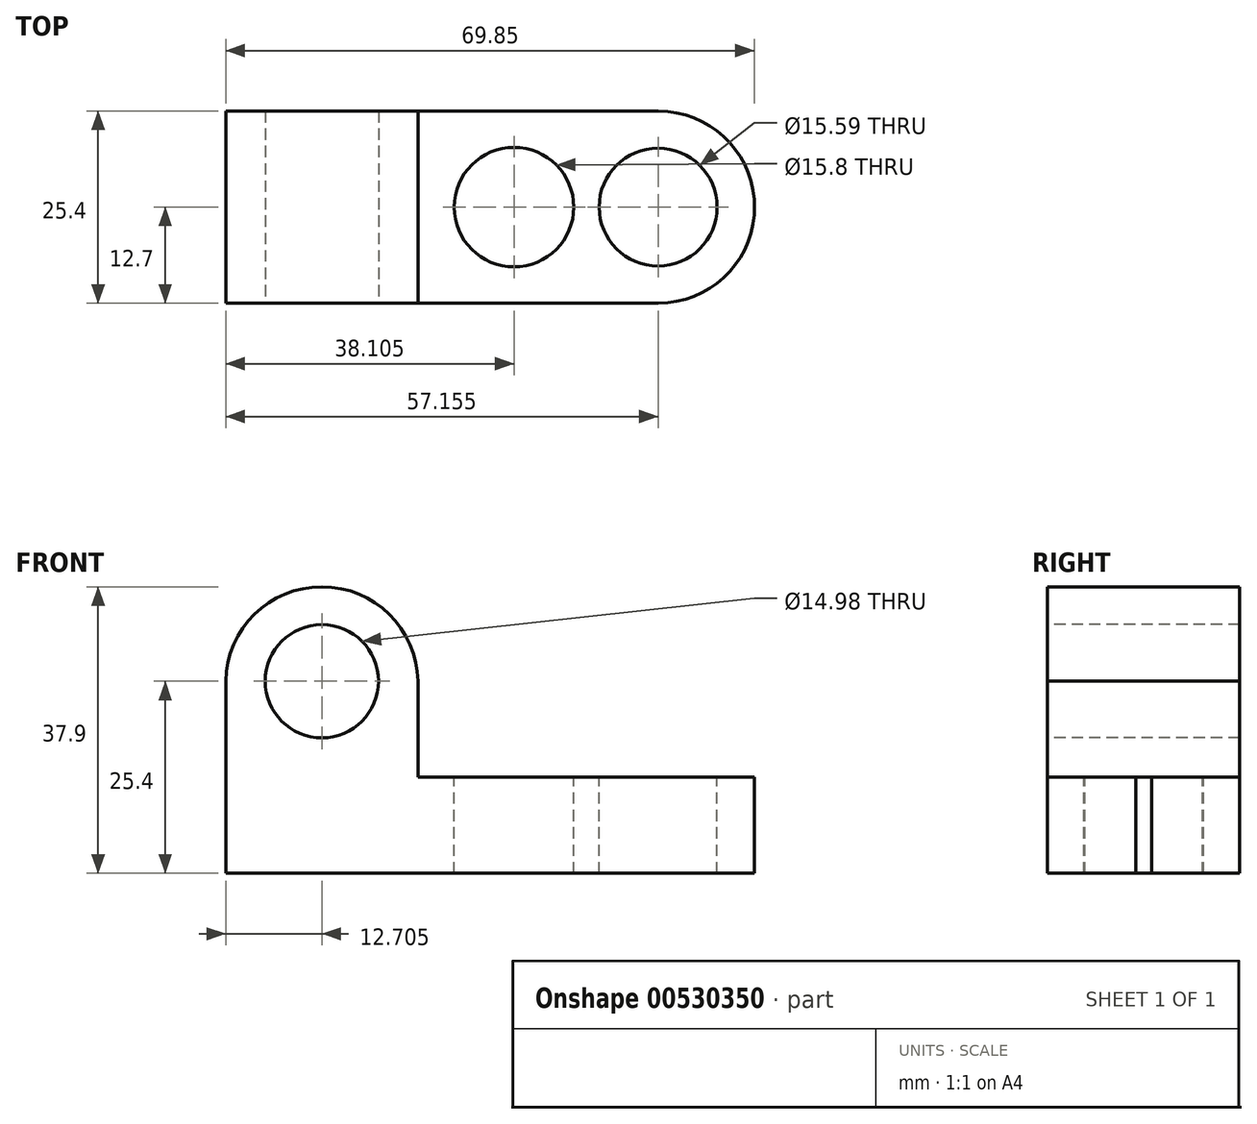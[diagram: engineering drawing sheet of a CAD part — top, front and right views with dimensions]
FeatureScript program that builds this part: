
annotation { "Feature Type Name" : "Feature", "Feature Type Description" : "" }
export const myFeature = defineFeature(function(context is Context, id is Id, definition is map)
    precondition{}
    {
        {
            var Q0;
            Q0=qCreatedBy(makeId("Front.planeOp"),FACE);
            var sketch = newSketch(context, id + "F0", { "sketchPlane" : qUnion([Q0])});
            skLineSegment(sketch, "E0", {"start": v(-78.95, 38.1) * mm, "end": v(-78.95, 0) * mm});
            skLineSegment(sketch, "E1", {"start": v(-78.95, 0) * mm, "end": v(-9.1, 0) * mm});
            skLineSegment(sketch, "E2", {"start": v(-9.1, 0) * mm, "end": v(-9.1, 12.7) * mm});
            skLineSegment(sketch, "E3", {"start": v(-9.1, 12.7) * mm, "end": v(-53.55, 12.7) * mm});
            skLineSegment(sketch, "E4", {"start": v(-53.55, 12.7) * mm, "end": v(-53.55, 38.1) * mm});
            skLineSegment(sketch, "E5", {"start": v(-53.55, 38.1) * mm, "end": v(-78.95, 38.1) * mm});
            skSolve(sketch);
        }
        {
            var Q0;
            Q0 = qSketchRegion(id + "F0", true);
            extrude(context, id + "F1", {"entities" : qUnion([Q0]), "depth" : 25.4 * mm, "offsetDistance" : 25.4 * mm});
        }
        {
            var Q0;
            Q0=makeQuery(id+"F1.opExtrude","CAP_FACE",FACE,{"disambiguationData":[OSD([sQuery(id+"F0.wireOp",EDGE,"E0"),sQuery(id+"F0.wireOp",EDGE,"E1"),sQuery(id+"F0.wireOp",EDGE,"E2"),sQuery(id+"F0.wireOp",EDGE,"E3"),sQuery(id+"F0.wireOp",EDGE,"E4"),sQuery(id+"F0.wireOp",EDGE,"E5")])],"isStart":false});
            var sketch = newSketch(context, id + "F2", { "sketchPlane" : qUnion([Q0])});
            skCircle(sketch, "E6", {"center": v(-66.25, 25.4) * mm, "radius": 7.5 * mm});
            skSolve(sketch);
        }
        {
            var Q0;
            Q0=makeQuery(id+"F2.imprint","IMPRINT",FACE,{"disambiguationData":[TD([[makeQuery(id+"F2.imprint","IMPRINT",EDGE,{"derivedFrom":sQuery(id+"F2.wireOp",EDGE,"E6")}),1.0]])]});
            extrude(context, id + "F3", {"entities" : qUnion([Q0]), "operationType" : NewBodyOperationType.REMOVE, "endBound" : BoundingType.THROUGH_ALL, "oppositeDirection" : true, "depth" : 25.4 * mm, "offsetDistance" : 25.4 * mm});
        }
        {
            var Q0;
            Q0=makeQuery(id+"F1.opExtrude","CAP_FACE",FACE,{"disambiguationData":[OSD([sQuery(id+"F0.wireOp",EDGE,"E0"),sQuery(id+"F0.wireOp",EDGE,"E1"),sQuery(id+"F0.wireOp",EDGE,"E2"),sQuery(id+"F0.wireOp",EDGE,"E3"),sQuery(id+"F0.wireOp",EDGE,"E4"),sQuery(id+"F0.wireOp",EDGE,"E5")])],"isStart":false});
            var sketch = newSketch(context, id + "F4", { "sketchPlane" : qUnion([Q0])});
            skArc(sketch, "E7", {"start": v(-53.55, 25.4) * mm, "mid": v(-66.25, 37.9) * mm, "end": v(-78.95, 25.4) * mm});
            skSolve(sketch);
        }
        {
            var Q0;
            Q0 = qSketchRegion(id + "F4", true);
            var Q1;
            {var subQ0=sQuery(id+"F4.wireOp",EDGE,"E7");Q1=makeQuery(id+"F4.imprint","IMPRINT",FACE,{"disambiguationData":[TD([[makeQuery(id+"F4.imprint","IMPRINT",EDGE,{"derivedFrom":subQ0}),-1.0]])]});}
            extrude(context, id + "F5", {"entities" : qUnion([Q0, Q1]), "operationType" : NewBodyOperationType.REMOVE, "endBound" : BoundingType.THROUGH_ALL, "oppositeDirection" : true, "depth" : 25.4 * mm, "offsetDistance" : 25.4 * mm});
        }
        {
            var Q0;
            Q0=makeQuery(id+"F1.opExtrude","SWEPT_FACE",FACE,{"disambiguationData":[OSD([sQuery(id+"F0.wireOp",EDGE,"E3")])]});
            var sketch = newSketch(context, id + "F6", { "sketchPlane" : qUnion([Q0])});
            skCircle(sketch, "E8", {"center": v(-40.85, -12.7) * mm, "radius": 7.9 * mm});
            skCircle(sketch, "E9", {"center": v(-21.8, -12.7) * mm, "radius": 7.8 * mm});
            skSolve(sketch);
        }
        {
            var Q0;
            Q0=makeQuery(id+"F6.imprint","IMPRINT",FACE,{"disambiguationData":[TD([[makeQuery(id+"F6.imprint","IMPRINT",EDGE,{"derivedFrom":sQuery(id+"F6.wireOp",EDGE,"E8")}),1.0]])]});
            var Q1;
            Q1=makeQuery(id+"F6.imprint","IMPRINT",FACE,{"disambiguationData":[TD([[makeQuery(id+"F6.imprint","IMPRINT",EDGE,{"derivedFrom":sQuery(id+"F6.wireOp",EDGE,"E9")}),1.0]])]});
            extrude(context, id + "F7", {"entities" : qUnion([Q0, Q1]), "operationType" : NewBodyOperationType.REMOVE, "endBound" : BoundingType.THROUGH_ALL, "oppositeDirection" : true, "depth" : 25.4 * mm, "offsetDistance" : 25.4 * mm});
        }
        {
            var Q0;
            Q0=makeQuery(id+"F1.opExtrude","SWEPT_FACE",FACE,{"disambiguationData":[OSD([sQuery(id+"F0.wireOp",EDGE,"E3")])]});
            var sketch = newSketch(context, id + "F8", { "sketchPlane" : qUnion([Q0])});
            skLineSegment(sketch, "E10", {"start": v(-40.69, -20.6) * mm, "end": v(-20.89, -20.44) * mm});
            skLineSegment(sketch, "E11", {"start": v(-40.9, -4.8) * mm, "end": v(-21.75, -4.9) * mm});
            skSolve(sketch);
        }
        {
            var Q0;
            Q0 = qSketchRegion(id + "F8", true);
            var Q1;
            {var subQ0=sQuery(id+"F8.wireOp",EDGE,"E10");var subQ1=makeQuery(id+"F7.boolean.opBoolean","COPY",EDGE,{"derivedFrom":makeQuery(id+"F7.opExtrude","CAP_EDGE",EDGE,{"disambiguationData":[OSD([sQuery(id+"F6.wireOp",EDGE,"E8")])],"isStart":true})});var subQ2=makeQuery(id+"F8.imprint","INTERSECT",VERTEX,{"derivedFrom":[subQ1,subQ0]});Q1=makeQuery(id+"F8.imprint","IMPRINT",FACE,{"disambiguationData":[TD([[makeQuery(id+"F8.imprint","IMPRINT",EDGE,{"disambiguationData":[TD([[subQ2,-1.0]])],"derivedFrom":subQ0}),1.0]])]});}
            extrude(context, id + "F9", {"entities" : qUnion([Q0, Q1]), "operationType" : NewBodyOperationType.REMOVE, "endBound" : BoundingType.THROUGH_ALL, "oppositeDirection" : true, "depth" : 25.4 * mm, "offsetDistance" : 25.4 * mm});
        }
        {
            var Q0;
            Q0=makeQuery(id+"F1.opExtrude","SWEPT_FACE",FACE,{"disambiguationData":[OSD([sQuery(id+"F0.wireOp",EDGE,"E3")])]});
            var sketch = newSketch(context, id + "F10", { "sketchPlane" : qUnion([Q0])});
            skArc(sketch, "E12", {"start": v(-21.75, -25.4) * mm, "mid": v(-9.05, -12.7) * mm, "end": v(-21.75, 0) * mm});
            skSolve(sketch);
        }
        {
            var Q0;
            Q0 = qSketchRegion(id + "F10", true);
            var Q1;
            {var subQ0=sQuery(id+"F10.wireOp",EDGE,"E12");var subQ1=sQuery(id+"F0.wireOp",EDGE,"E3");var subQ2=makeQuery(id+"F1.opExtrude","CAP_EDGE",EDGE,{"disambiguationData":[OSD([subQ1])],"isStart":true});var subQ3=makeQuery(id+"F10.imprint","INTERSECT",VERTEX,{"derivedFrom":[subQ2,subQ0]});Q1=makeQuery(id+"F10.imprint","IMPRINT",FACE,{"disambiguationData":[TD([[makeQuery(id+"F10.imprint","IMPRINT",EDGE,{"disambiguationData":[TD([[subQ3,1.0]])],"derivedFrom":subQ0}),-1.0]])]});}
            var Q2;
            {var subQ0=sQuery(id+"F10.wireOp",EDGE,"E12");var subQ1=sQuery(id+"F0.wireOp",EDGE,"E3");var subQ2=makeQuery(id+"F1.opExtrude","CAP_EDGE",EDGE,{"disambiguationData":[OSD([subQ1])],"isStart":false});var subQ3=makeQuery(id+"F10.imprint","INTERSECT",VERTEX,{"derivedFrom":[subQ2,subQ0]});Q2=makeQuery(id+"F10.imprint","IMPRINT",FACE,{"disambiguationData":[TD([[makeQuery(id+"F10.imprint","IMPRINT",EDGE,{"disambiguationData":[TD([[subQ3,-1.0]])],"derivedFrom":subQ0}),-1.0]])]});}
            extrude(context, id + "F11", {"entities" : qUnion([Q0, Q1, Q2]), "operationType" : NewBodyOperationType.REMOVE, "endBound" : BoundingType.THROUGH_ALL, "oppositeDirection" : true, "depth" : 25.4 * mm, "offsetDistance" : 25.4 * mm});
        }
    });
